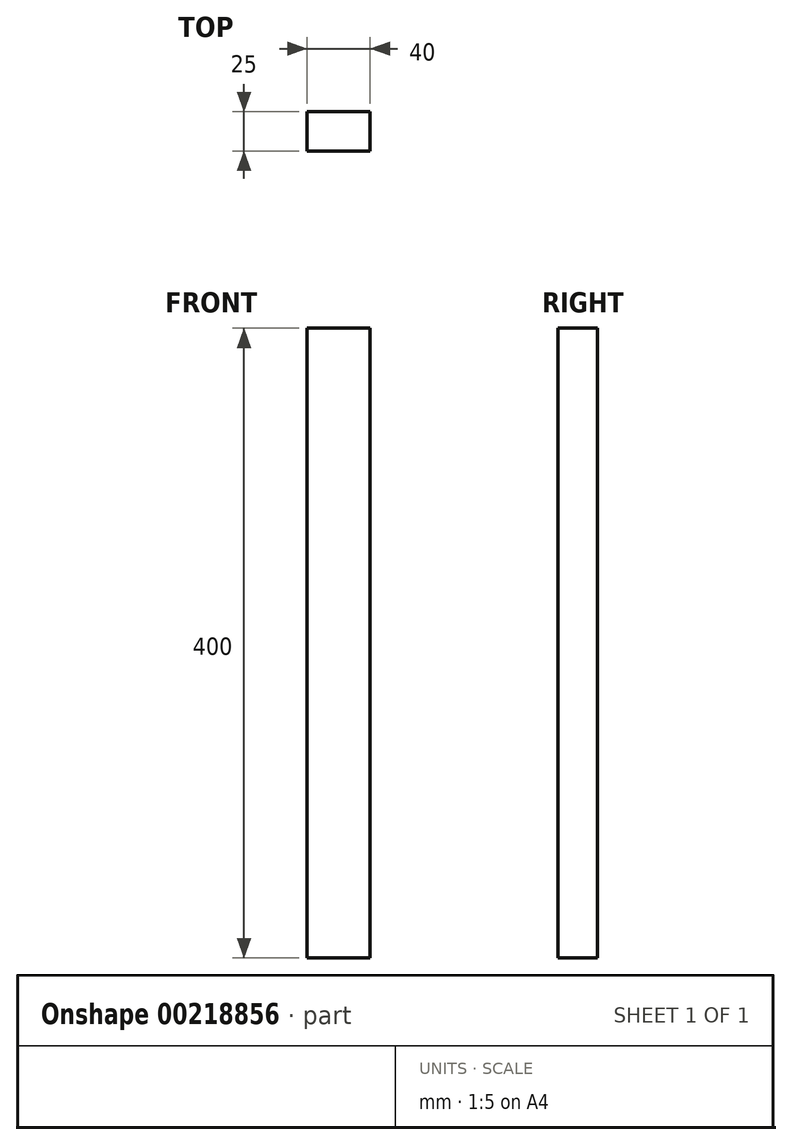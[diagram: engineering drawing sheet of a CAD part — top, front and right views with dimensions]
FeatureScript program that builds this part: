
annotation { "Feature Type Name" : "Feature", "Feature Type Description" : "" }
export const myFeature = defineFeature(function(context is Context, id is Id, definition is map)
    precondition{}
    {
        {
            var Q0;
            Q0=qCreatedBy(makeId("Top.planeOp"),FACE);
            var sketch = newSketch(context, id + "F0", { "sketchPlane" : qUnion([Q0])});
            skLineSegment(sketch, "E0.bottom", {"start": v(20, -12.5) * mm, "end": v(-20, -12.5) * mm});
            skLineSegment(sketch, "E0.top", {"start": v(20, 12.5) * mm, "end": v(-20, 12.5) * mm});
            skLineSegment(sketch, "E0.left", {"start": v(20, -12.5) * mm, "end": v(20, 12.5) * mm});
            skLineSegment(sketch, "E0.right", {"start": v(-20, -12.5) * mm, "end": v(-20, 12.5) * mm});
            skPoint(sketch, "E0.middle", {"position": v(0, 0) * mm});
            skSolve(sketch);
        }
        {
            var Q0;
            Q0=makeQuery(id+"F0.imprint","IMPRINT",FACE,{"disambiguationData":[TD([[makeQuery(id+"F0.imprint","IMPRINT",EDGE,{"derivedFrom":sQuery(id+"F0.wireOp",EDGE,"E0.bottom")}),-1.0]])]});
            extrude(context, id + "F1", {"entities" : qUnion([Q0]), "depth" : 400 * mm});
        }
    });
